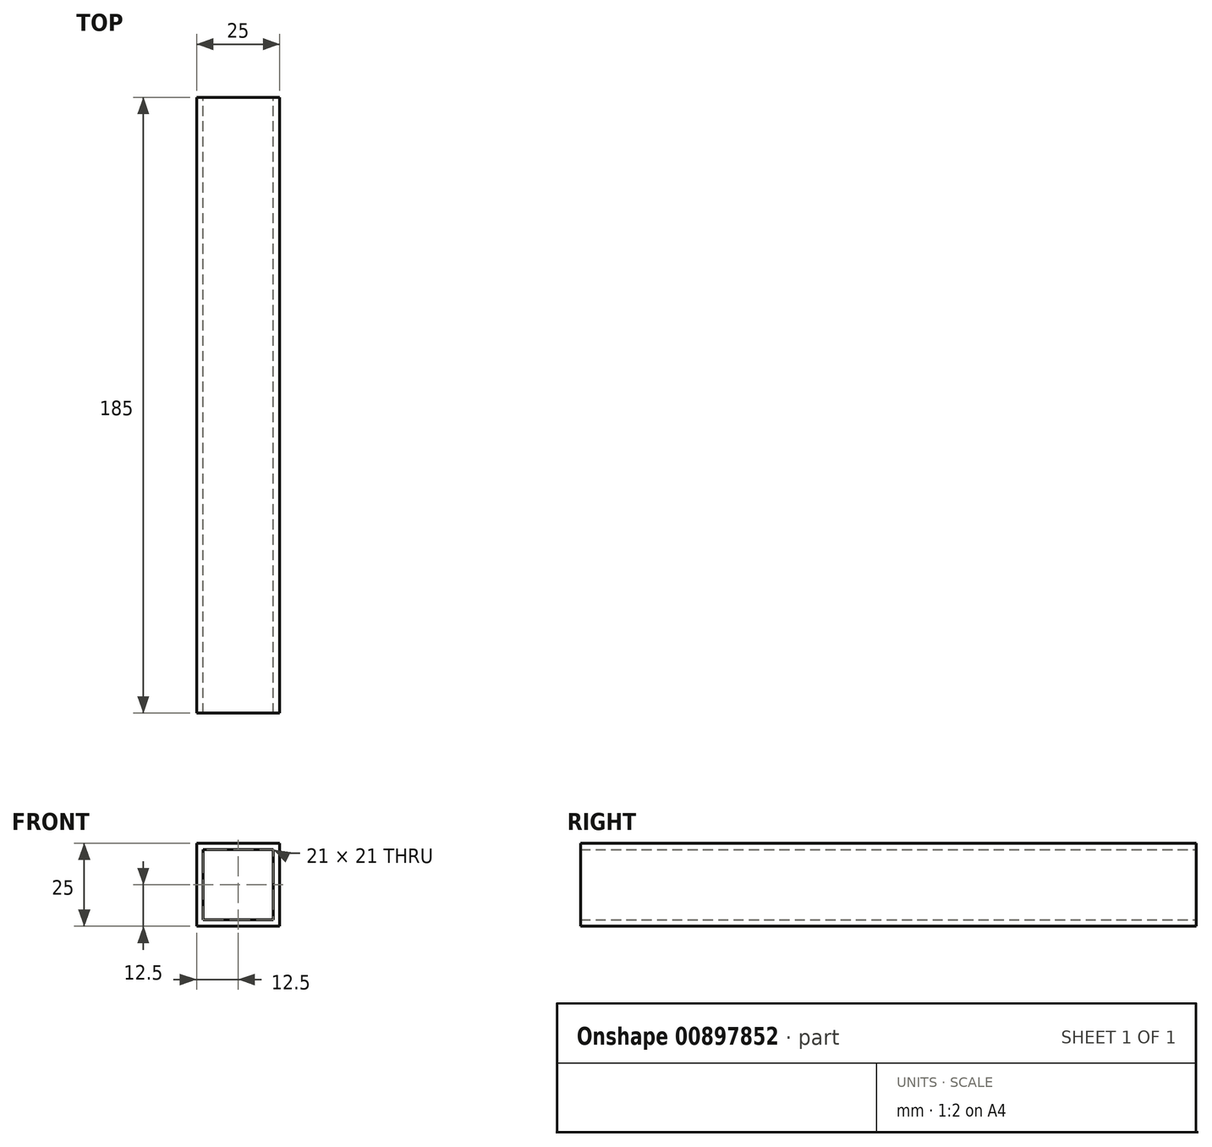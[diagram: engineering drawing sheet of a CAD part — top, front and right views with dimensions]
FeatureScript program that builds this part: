
annotation { "Feature Type Name" : "Feature", "Feature Type Description" : "" }
export const myFeature = defineFeature(function(context is Context, id is Id, definition is map)
    precondition{}
    {
        {
            var Q0;
            Q0=qCreatedBy(makeId("Front.planeOp"),FACE);
            var sketch = newSketch(context, id + "F0", { "sketchPlane" : qUnion([Q0])});
            skLineSegment(sketch, "E0.bottom", {"start": v(12.5, -12.5) * mm, "end": v(-12.5, -12.5) * mm});
            skLineSegment(sketch, "E0.top", {"start": v(12.5, 12.5) * mm, "end": v(-12.5, 12.5) * mm});
            skLineSegment(sketch, "E0.left", {"start": v(12.5, -12.5) * mm, "end": v(12.5, 12.5) * mm});
            skLineSegment(sketch, "E0.right", {"start": v(-12.5, -12.5) * mm, "end": v(-12.5, 12.5) * mm});
            skPoint(sketch, "E0.middle", {"position": v(0, 0) * mm});
            skLineSegment(sketch, "E1.0", {"start": v(10.5, 10.5) * mm, "end": v(-10.5, 10.5) * mm});
            skLineSegment(sketch, "E1.1", {"start": v(10.5, -10.5) * mm, "end": v(10.5, 10.5) * mm});
            skLineSegment(sketch, "E1.2", {"start": v(10.5, -10.5) * mm, "end": v(-10.5, -10.5) * mm});
            skLineSegment(sketch, "E1.3", {"start": v(-10.5, -10.5) * mm, "end": v(-10.5, 10.5) * mm});
            skSolve(sketch);
        }
        {
            var Q0;
            Q0=qSketchRegion(id+"F0",true);
            extrude(context, id + "F1", {"entities" : qUnion([Q0]), "depth" : 92.5 * mm, "offsetDistance" : 25 * mm, "hasSecondDirection" : true, "secondDirectionOppositeDirection" : true, "secondDirectionDepth" : 92.5 * mm});
        }
    });
